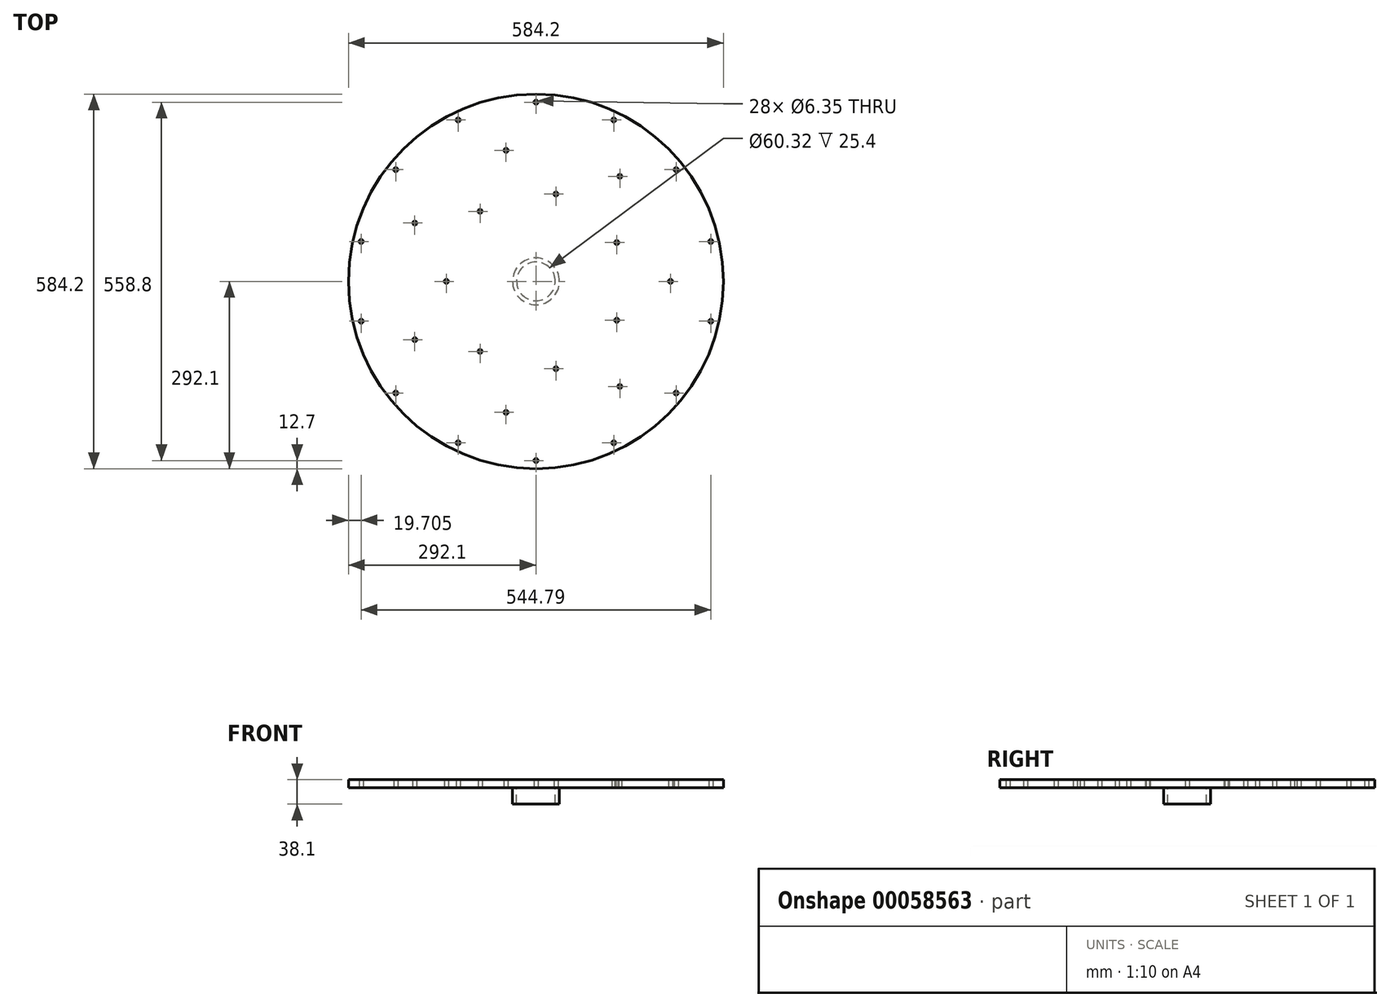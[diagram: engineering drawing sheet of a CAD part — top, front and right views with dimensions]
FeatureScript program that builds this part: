
annotation { "Feature Type Name" : "Feature", "Feature Type Description" : "" }
export const myFeature = defineFeature(function(context is Context, id is Id, definition is map)
    precondition{}
    {
        {
            var Q0;
            Q0=qCreatedBy(makeId("Top.planeOp"),FACE);
            var sketch = newSketch(context, id + "F0", { "sketchPlane" : qUnion([Q0])});
            skCircle(sketch, "E0", {"center": v(0, 0) * mm, "radius": 279.4 * mm});
            skCircle(sketch, "E1", {"center": v(0, 0) * mm, "radius": 292.1 * mm});
            skCircle(sketch, "E2", {"center": v(0, 0) * mm, "radius": 139.7 * mm});
            skCircle(sketch, "E3", {"center": v(0, 0) * mm, "radius": 209.55 * mm});
            skLineSegment(sketch, "E4.trimOffspring", {"start": v(-163.83, 130.65) * mm, "end": v(-218.44, 174.2) * mm});
            skLineSegment(sketch, "E5.trimOffspring", {"start": v(-90.92, 188.8) * mm, "end": v(-121.23, 251.73) * mm});
            skLineSegment(sketch, "E6.trimOffspring", {"start": v(0, 209.55) * mm, "end": v(0, 279.4) * mm});
            skLineSegment(sketch, "E7.trimOffspring", {"start": v(90.92, 188.8) * mm, "end": v(121.23, 251.73) * mm});
            skLineSegment(sketch, "E8.trimOffspring", {"start": v(163.83, 130.65) * mm, "end": v(218.44, 174.2) * mm});
            skLineSegment(sketch, "E9.trimOffspring", {"start": v(204.3, 46.63) * mm, "end": v(272.4, 62.17) * mm});
            skLineSegment(sketch, "E10.trimOffspring", {"start": v(204.3, -46.63) * mm, "end": v(272.4, -62.17) * mm});
            skLineSegment(sketch, "E11.trimOffspring", {"start": v(163.83, -130.65) * mm, "end": v(218.44, -174.2) * mm});
            skLineSegment(sketch, "E12.trimOffspring", {"start": v(90.92, -188.8) * mm, "end": v(121.23, -251.73) * mm});
            skLineSegment(sketch, "E13.trimOffspring", {"start": v(0, -209.55) * mm, "end": v(0, -279.4) * mm});
            skLineSegment(sketch, "E14.trimOffspring", {"start": v(-90.92, -188.8) * mm, "end": v(-121.23, -251.73) * mm});
            skLineSegment(sketch, "E15.trimOffspring", {"start": v(-163.83, -130.65) * mm, "end": v(-218.44, -174.2) * mm});
            skLineSegment(sketch, "E16.trimOffspring", {"start": v(-204.3, -46.63) * mm, "end": v(-272.4, -62.17) * mm});
            skLineSegment(sketch, "E17.trimOffspring", {"start": v(-204.3, 46.63) * mm, "end": v(-272.4, 62.17) * mm});
            skLineSegment(sketch, "E18", {"start": v(139.7, 0) * mm, "end": v(209.55, 0) * mm});
            skLineSegment(sketch, "E19.1.0", {"start": v(87.1, 109.22) * mm, "end": v(130.65, 163.83) * mm});
            skLineSegment(sketch, "E19.2.0", {"start": v(-31.09, 136.2) * mm, "end": v(-46.63, 204.3) * mm});
            skLineSegment(sketch, "E19.3.0", {"start": v(-125.87, 60.61) * mm, "end": v(-188.8, 90.92) * mm});
            skLineSegment(sketch, "E19.4.0", {"start": v(-125.87, -60.61) * mm, "end": v(-188.8, -90.92) * mm});
            skLineSegment(sketch, "E19.5.0", {"start": v(-31.09, -136.2) * mm, "end": v(-46.63, -204.3) * mm});
            skLineSegment(sketch, "E19.6.0", {"start": v(87.1, -109.22) * mm, "end": v(130.65, -163.83) * mm});
            skLineSegment(sketch, "E20", {"start": v(0, 0) * mm, "end": v(-139.7, 0) * mm});
            skLineSegment(sketch, "E21.1.0", {"start": v(0, 0) * mm, "end": v(-87.1, -109.22) * mm});
            skLineSegment(sketch, "E21.2.0", {"start": v(0, 0) * mm, "end": v(31.09, -136.2) * mm});
            skLineSegment(sketch, "E21.3.0", {"start": v(0, 0) * mm, "end": v(125.87, -60.61) * mm});
            skLineSegment(sketch, "E21.4.0", {"start": v(0, 0) * mm, "end": v(125.87, 60.61) * mm});
            skLineSegment(sketch, "E21.5.0", {"start": v(0, 0) * mm, "end": v(31.09, 136.2) * mm});
            skLineSegment(sketch, "E21.6.0", {"start": v(0, 0) * mm, "end": v(-87.1, 109.22) * mm});
            skSolve(sketch);
        }
        {
            var Q0;
            {var subQ0=sQuery(id+"F0.wireOp",EDGE,"E4.trimOffspring");Q0=makeQuery(id+"F0.imprint","IMPRINT",FACE,{"disambiguationData":[TD([[makeQuery(id+"F0.imprint","IMPRINT",EDGE,{"derivedFrom":subQ0}),-1.0]])]});}
            var Q1;
            {var subQ0=sQuery(id+"F0.wireOp",EDGE,"E6.trimOffspring");Q1=makeQuery(id+"F0.imprint","IMPRINT",FACE,{"disambiguationData":[TD([[makeQuery(id+"F0.imprint","IMPRINT",EDGE,{"derivedFrom":subQ0}),-1.0]])]});}
            var Q2;
            {var subQ2=sQuery(id+"F0.wireOp",EDGE,"E21.5.0");Q2=makeQuery(id+"F0.imprint","IMPRINT",FACE,{"disambiguationData":[TD([[makeQuery(id+"F0.imprint","IMPRINT",EDGE,{"derivedFrom":subQ2}),1.0]])]});}
            var Q3;
            {var subQ0=sQuery(id+"F0.wireOp",EDGE,"E9.trimOffspring");Q3=makeQuery(id+"F0.imprint","IMPRINT",FACE,{"disambiguationData":[TD([[makeQuery(id+"F0.imprint","IMPRINT",EDGE,{"derivedFrom":subQ0}),-1.0]])]});}
            var Q4;
            {var subQ0=sQuery(id+"F0.wireOp",EDGE,"E13.trimOffspring");Q4=makeQuery(id+"F0.imprint","IMPRINT",FACE,{"disambiguationData":[TD([[makeQuery(id+"F0.imprint","IMPRINT",EDGE,{"derivedFrom":subQ0}),-1.0]])]});}
            var Q5;
            {var subQ2=sQuery(id+"F0.wireOp",EDGE,"E21.2.0");Q5=makeQuery(id+"F0.imprint","IMPRINT",FACE,{"disambiguationData":[TD([[makeQuery(id+"F0.imprint","IMPRINT",EDGE,{"derivedFrom":subQ2}),1.0]])]});}
            var Q6;
            {var subQ2=sQuery(id+"F0.wireOp",EDGE,"E21.1.0");Q6=makeQuery(id+"F0.imprint","IMPRINT",FACE,{"disambiguationData":[TD([[makeQuery(id+"F0.imprint","IMPRINT",EDGE,{"derivedFrom":subQ2}),1.0]])]});}
            var Q7;
            {var subQ0=sQuery(id+"F0.wireOp",EDGE,"E5.trimOffspring");Q7=makeQuery(id+"F0.imprint","IMPRINT",FACE,{"disambiguationData":[TD([[makeQuery(id+"F0.imprint","IMPRINT",EDGE,{"derivedFrom":subQ0}),-1.0]])]});}
            var Q8;
            {var subQ0=sQuery(id+"F0.wireOp",EDGE,"E10.trimOffspring");Q8=makeQuery(id+"F0.imprint","IMPRINT",FACE,{"disambiguationData":[TD([[makeQuery(id+"F0.imprint","IMPRINT",EDGE,{"derivedFrom":subQ0}),-1.0]])]});}
            var Q9;
            {var subQ4=sQuery(id+"F0.wireOp",EDGE,"E19.2.0");Q9=makeQuery(id+"F0.imprint","IMPRINT",FACE,{"disambiguationData":[TD([[makeQuery(id+"F0.imprint","IMPRINT",EDGE,{"derivedFrom":subQ4}),1.0]])]});}
            var Q10;
            {var subQ3=sQuery(id+"F0.wireOp",EDGE,"E7.trimOffspring");Q10=makeQuery(id+"F0.imprint","IMPRINT",FACE,{"disambiguationData":[TD([[makeQuery(id+"F0.imprint","IMPRINT",EDGE,{"derivedFrom":subQ3}),-1.0]])]});}
            var Q11;
            {var subQ3=sQuery(id+"F0.wireOp",EDGE,"E19.1.0");Q11=makeQuery(id+"F0.imprint","IMPRINT",FACE,{"disambiguationData":[TD([[makeQuery(id+"F0.imprint","IMPRINT",EDGE,{"derivedFrom":subQ3}),1.0]])]});}
            var Q12;
            Q12=makeQuery(id+"F0.imprint","IMPRINT",FACE,{"disambiguationData":[TD([[makeQuery(id+"F0.imprint","IMPRINT",EDGE,{"derivedFrom":sQuery(id+"F0.wireOp",EDGE,"E1")}),1.0]])]});
            var Q13;
            {var subQ3=sQuery(id+"F0.wireOp",EDGE,"E21.3.0");Q13=makeQuery(id+"F0.imprint","IMPRINT",FACE,{"disambiguationData":[TD([[makeQuery(id+"F0.imprint","IMPRINT",EDGE,{"derivedFrom":subQ3}),1.0]])]});}
            var Q14;
            {var subQ2=sQuery(id+"F0.wireOp",EDGE,"E21.4.0");Q14=makeQuery(id+"F0.imprint","IMPRINT",FACE,{"disambiguationData":[TD([[makeQuery(id+"F0.imprint","IMPRINT",EDGE,{"derivedFrom":subQ2}),1.0]])]});}
            var Q15;
            {var subQ3=sQuery(id+"F0.wireOp",EDGE,"E19.5.0");Q15=makeQuery(id+"F0.imprint","IMPRINT",FACE,{"disambiguationData":[TD([[makeQuery(id+"F0.imprint","IMPRINT",EDGE,{"derivedFrom":subQ3}),1.0]])]});}
            var Q16;
            {var subQ0=sQuery(id+"F0.wireOp",EDGE,"E15.trimOffspring");Q16=makeQuery(id+"F0.imprint","IMPRINT",FACE,{"disambiguationData":[TD([[makeQuery(id+"F0.imprint","IMPRINT",EDGE,{"derivedFrom":subQ0}),-1.0]])]});}
            var Q17;
            {var subQ4=sQuery(id+"F0.wireOp",EDGE,"E18");Q17=makeQuery(id+"F0.imprint","IMPRINT",FACE,{"disambiguationData":[TD([[makeQuery(id+"F0.imprint","IMPRINT",EDGE,{"derivedFrom":subQ4}),-1.0]])]});}
            var Q18;
            {var subQ3=sQuery(id+"F0.wireOp",EDGE,"E19.3.0");Q18=makeQuery(id+"F0.imprint","IMPRINT",FACE,{"disambiguationData":[TD([[makeQuery(id+"F0.imprint","IMPRINT",EDGE,{"derivedFrom":subQ3}),1.0]])]});}
            var Q19;
            {var subQ0=sQuery(id+"F0.wireOp",EDGE,"E16.trimOffspring");Q19=makeQuery(id+"F0.imprint","IMPRINT",FACE,{"disambiguationData":[TD([[makeQuery(id+"F0.imprint","IMPRINT",EDGE,{"derivedFrom":subQ0}),-1.0]])]});}
            var Q20;
            {var subQ0=sQuery(id+"F0.wireOp",EDGE,"E8.trimOffspring");Q20=makeQuery(id+"F0.imprint","IMPRINT",FACE,{"disambiguationData":[TD([[makeQuery(id+"F0.imprint","IMPRINT",EDGE,{"derivedFrom":subQ0}),-1.0]])]});}
            var Q21;
            {var subQ0=sQuery(id+"F0.wireOp",EDGE,"E11.trimOffspring");Q21=makeQuery(id+"F0.imprint","IMPRINT",FACE,{"disambiguationData":[TD([[makeQuery(id+"F0.imprint","IMPRINT",EDGE,{"derivedFrom":subQ0}),-1.0]])]});}
            var Q22;
            {var subQ0=sQuery(id+"F0.wireOp",EDGE,"E12.trimOffspring");Q22=makeQuery(id+"F0.imprint","IMPRINT",FACE,{"disambiguationData":[TD([[makeQuery(id+"F0.imprint","IMPRINT",EDGE,{"derivedFrom":subQ0}),-1.0]])]});}
            var Q23;
            {var subQ0=sQuery(id+"F0.wireOp",EDGE,"E14.trimOffspring");Q23=makeQuery(id+"F0.imprint","IMPRINT",FACE,{"disambiguationData":[TD([[makeQuery(id+"F0.imprint","IMPRINT",EDGE,{"derivedFrom":subQ0}),-1.0]])]});}
            var Q24;
            {var subQ3=sQuery(id+"F0.wireOp",EDGE,"E4.trimOffspring");Q24=makeQuery(id+"F0.imprint","IMPRINT",FACE,{"disambiguationData":[TD([[makeQuery(id+"F0.imprint","IMPRINT",EDGE,{"derivedFrom":subQ3}),1.0]])]});}
            var Q25;
            {var subQ6=sQuery(id+"F0.wireOp",EDGE,"E18");Q25=makeQuery(id+"F0.imprint","IMPRINT",FACE,{"disambiguationData":[TD([[makeQuery(id+"F0.imprint","IMPRINT",EDGE,{"derivedFrom":subQ6}),1.0]])]});}
            var Q26;
            {var subQ3=sQuery(id+"F0.wireOp",EDGE,"E20");Q26=makeQuery(id+"F0.imprint","IMPRINT",FACE,{"disambiguationData":[TD([[makeQuery(id+"F0.imprint","IMPRINT",EDGE,{"derivedFrom":subQ3}),-1.0]])]});}
            var Q27;
            {var subQ2=sQuery(id+"F0.wireOp",EDGE,"E20");Q27=makeQuery(id+"F0.imprint","IMPRINT",FACE,{"disambiguationData":[TD([[makeQuery(id+"F0.imprint","IMPRINT",EDGE,{"derivedFrom":subQ2}),1.0]])]});}
            var Q28;
            {var subQ3=sQuery(id+"F0.wireOp",EDGE,"E19.4.0");Q28=makeQuery(id+"F0.imprint","IMPRINT",FACE,{"disambiguationData":[TD([[makeQuery(id+"F0.imprint","IMPRINT",EDGE,{"derivedFrom":subQ3}),1.0]])]});}
            extrude(context, id + "F1", {"entities" : qUnion([Q0, Q1, Q2, Q3, Q4, Q5, Q6, Q7, Q8, Q9, Q10, Q11, Q12, Q13, Q14, Q15, Q16, Q17, Q18, Q19, Q20, Q21, Q22, Q23, Q24, Q25, Q26, Q27, Q28]), "depth" : 12.7 * mm});
        }
        {
            var Q0;
            Q0=sQuery(id+"F0.wireOp",VERTEX,"E4.trimOffspring.end");
            var Q1;
            Q1=sQuery(id+"F0.wireOp",VERTEX,"E5.trimOffspring.end");
            var Q2;
            Q2=sQuery(id+"F0.wireOp",VERTEX,"E6.trimOffspring.end");
            var Q3;
            Q3=sQuery(id+"F0.wireOp",VERTEX,"E7.trimOffspring.end");
            var Q4;
            Q4=sQuery(id+"F0.wireOp",VERTEX,"E8.trimOffspring.end");
            var Q5;
            Q5=sQuery(id+"F0.wireOp",VERTEX,"E9.trimOffspring.end");
            var Q6;
            Q6=sQuery(id+"F0.wireOp",VERTEX,"E10.trimOffspring.end");
            var Q7;
            Q7=sQuery(id+"F0.wireOp",VERTEX,"E11.trimOffspring.end");
            var Q8;
            Q8=sQuery(id+"F0.wireOp",VERTEX,"E12.trimOffspring.end");
            var Q9;
            Q9=sQuery(id+"F0.wireOp",VERTEX,"E13.trimOffspring.end");
            var Q10;
            Q10=sQuery(id+"F0.wireOp",VERTEX,"E14.trimOffspring.end");
            var Q11;
            Q11=sQuery(id+"F0.wireOp",VERTEX,"E15.trimOffspring.end");
            var Q12;
            Q12=sQuery(id+"F0.wireOp",VERTEX,"E16.trimOffspring.end");
            var Q13;
            Q13=sQuery(id+"F0.wireOp",VERTEX,"E17.trimOffspring.end");
            var Q14;
            Q14=sQuery(id+"F0.wireOp",VERTEX,"E19.3.0.end");
            var Q15;
            Q15=sQuery(id+"F0.wireOp",VERTEX,"E19.2.0.end");
            var Q16;
            Q16=sQuery(id+"F0.wireOp",VERTEX,"E19.1.0.end");
            var Q17;
            Q17=sQuery(id+"F0.wireOp",VERTEX,"E18.end");
            var Q18;
            Q18=sQuery(id+"F0.wireOp",VERTEX,"E19.6.0.end");
            var Q19;
            Q19=sQuery(id+"F0.wireOp",VERTEX,"E19.5.0.end");
            var Q20;
            Q20=sQuery(id+"F0.wireOp",VERTEX,"E19.4.0.end");
            var Q21;
            Q21=sQuery(id+"F0.wireOp",VERTEX,"E20.end");
            var Q22;
            Q22=sQuery(id+"F0.wireOp",VERTEX,"E21.6.0.end");
            var Q23;
            Q23=sQuery(id+"F0.wireOp",VERTEX,"E21.5.0.end");
            var Q24;
            Q24=sQuery(id+"F0.wireOp",VERTEX,"E21.4.0.end");
            var Q25;
            Q25=sQuery(id+"F0.wireOp",VERTEX,"E21.3.0.end");
            var Q26;
            Q26=sQuery(id+"F0.wireOp",VERTEX,"E21.2.0.end");
            var Q27;
            Q27=sQuery(id+"F0.wireOp",VERTEX,"E21.1.0.end");
            var Q28;
            Q28=makeQuery(id+"F1.opExtrude","SWEPT_BODY",BODY,{"disambiguationData":[OSD([sQuery(id+"F0.wireOp",EDGE,"E1")])]});
            hole(context, id + "F2", {"style" : HoleStyle.SIMPLE, "holeDiameter" : 6.35 * mm, "endStyle" : HoleEndStyle.THROUGH, "oppositeDirection" : true, "locations" : qUnion([Q0, Q1, Q2, Q3, Q4, Q5, Q6, Q7, Q8, Q9, Q10, Q11, Q12, Q13, Q14, Q15, Q16, Q17, Q18, Q19, Q20, Q21, Q22, Q23, Q24, Q25, Q26, Q27]), "scope" : qUnion([Q28])});
        }
        {
            var Q0;
            Q0=makeQuery(id+"F1.opExtrude","CAP_FACE",FACE,{"disambiguationData":[OSD([sQuery(id+"F0.wireOp",EDGE,"E1")])],"isStart":true});
            var sketch = newSketch(context, id + "F3", { "sketchPlane" : qUnion([Q0])});
            skCircle(sketch, "E22", {"center": v(0, 0) * mm, "radius": 36.51 * mm});
            skCircle(sketch, "E23", {"center": v(0, 0) * mm, "radius": 30.16 * mm});
            skSolve(sketch);
        }
        {
            var Q0;
            Q0 = qSketchRegion(id + "F3", true);
            extrude(context, id + "F4", {"entities" : qUnion([Q0]), "operationType" : NewBodyOperationType.ADD, "depth" : 25.4 * mm});
        }
    });
